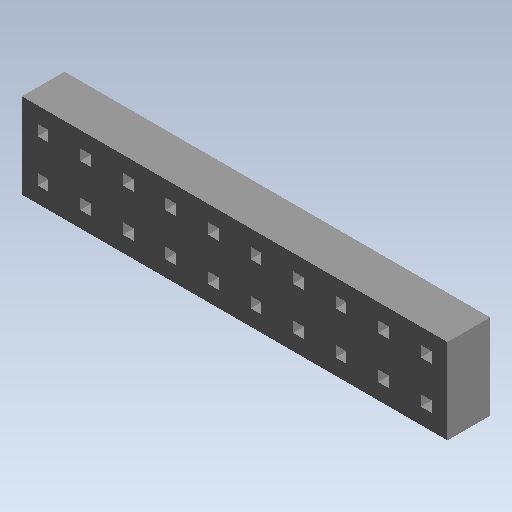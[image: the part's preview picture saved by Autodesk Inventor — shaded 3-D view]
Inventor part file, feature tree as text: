
AUTODESK INVENTOR PART (.ipt)
format: ipt  version: 2021 (Build 250183000, 183)  size: 187,392 bytes
history: native  units: mm (DEFAULTED — no unit token found)
features: other x7, extrude x1, sketch x1
ambient origin geometry x8: Origin, YZ Plane, XZ Plane, XY Plane, X Axis, Y Axis, Z Axis, Center Point
bodies: Solid1 (feature_tree)
feature tree (9):
  extrude  "Extrusion1"  TaperAngle=0.0deg  [1 undecoded]
  other  "0_XY"
  other  "0_YZ"
  other  "0_ZX"
  other  "0_X"
  other  "0_Y"
  other  "0_Z"
  other  "0_Center"
  sketch  "Sketch0"  dims[d0=2.0066mm d1=0.0mm d2=0.0mm]
note: 1 required parameter value undecoded (feature->parameter linkage not recoverable at this tier; creation-order binding heuristic only, values carry confidence <= 0.55)
